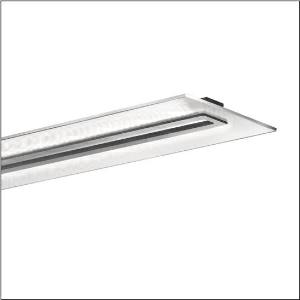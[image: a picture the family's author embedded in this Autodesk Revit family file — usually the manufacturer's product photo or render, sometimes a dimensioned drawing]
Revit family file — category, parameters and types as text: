
# Revit family: vega_r__11_5mn238dle_9bfa
name_source: partatom
category: Lighting Fixtures
units: mm (PartAtom-declared; Revit-internal decimal feet)

## family parameters
Cut with Voids When Loaded = No
Host = Face
Light Source = No
Part Type = Normal
Room Calculation Point = No
Round Connector Dimension = Use Diameter
Shared = No

## types (1)
- --- (1 x LED 4000K / CRI = 80 (unbekannt), 8130 lm, 4000K)
    Apparent Load = 62 VA
    CIE Flux Codes = 61 86 97 62 100
    Color Rendering = 80
    Color Temperature = 4000K
    Default Elevation = 1800 mm
    Description = Vega® 11, office luminaire, primary light control with prismatic reflector, of PMMA, transparent prismatic structure, CAT 2 (L<= 1500cd/m²), light emission: direct/indirect distribution, primary light characteristic: symmetric, installation type: suspended mounting, surface-mounted, LED, rated luminous flux: 8.130lm, luminous efficacy: 131lm/W, light colour: 840, colour temperature: 4000K, control gear: ECG, with terminal, 3+2-pole, max. 2.5mm², mains connection: 230V, AC, 50Hz, connection cable inclusive, cable length: 1,5m, rated input power: 62W, luminaire housing, rectangular, rounded, of aluminium section, anodised, metallic grey (RAL 9006), length: 1.250mm, width: 350mm, height: 43mm, luminaire housing, lower part, of aluminium section, anodised, metallic grey (RAL 9006), of PC, grey, protection rating (complete): IP20, insulation class (complete): insulation class I (protective earthing), certification: CE, standard: EN 50419, packaging unit: 1 piece
    Height = 40 mm  [stored 0.131234 ft]
    Lamp = 1 x LED 4000K / CRI >= 80 (unbekannt)
    Lamp Light Flux = 8130 lm
    Lamp count = 1
    Length = 1250 mm
    Luminous efficacy = 131 lm/W
    Manufacturer = Siteco
    ModVariant = No
    Model = 5MN238DLE
    Mounting Place = Ceiling
    Mounting Type = Pendant
    Number of Poles = 1
    OnlyDefault = Yes
    Power Factor = 1
    Product Name = Vega® 11
    Product group = office luminaire | ceiling pendant
    ProductGroupID = 902
    Protection Class = Protection class I
    Protection Degree = IP 20
    RLX_Detail_Level = 1
    RLX_Emergency_Light_Flux = 0 lm
    RLX_Emergency_Type = 0
    RLX_Emergency_Type_DB = No
    RlxData = <blob elided: 62937 chars, md5=99d7eac0>
    Socket = socket
    Standby Power = 0 W
    System Light Flux = 8130 lm
    System Power = 62 W
    Type Comments = factory setting: luminous flux: 100 % | dim-lin: 254 | 458 mA
    Type Image = l_1004807.jpg
    URL = http://relux.com
    VarID = @adj_149957
    Voltage = 0 V
    Weight = 0.00 kg
    Width = 350 mm

note: [stored X ft] marks values corroborated as IEEE doubles in the binary element streams (Revit-internal decimal feet)

## geometry (parser evidence)
native form markers: Blend x4, Sweep x16
no freeform markers — native parametric forms only
